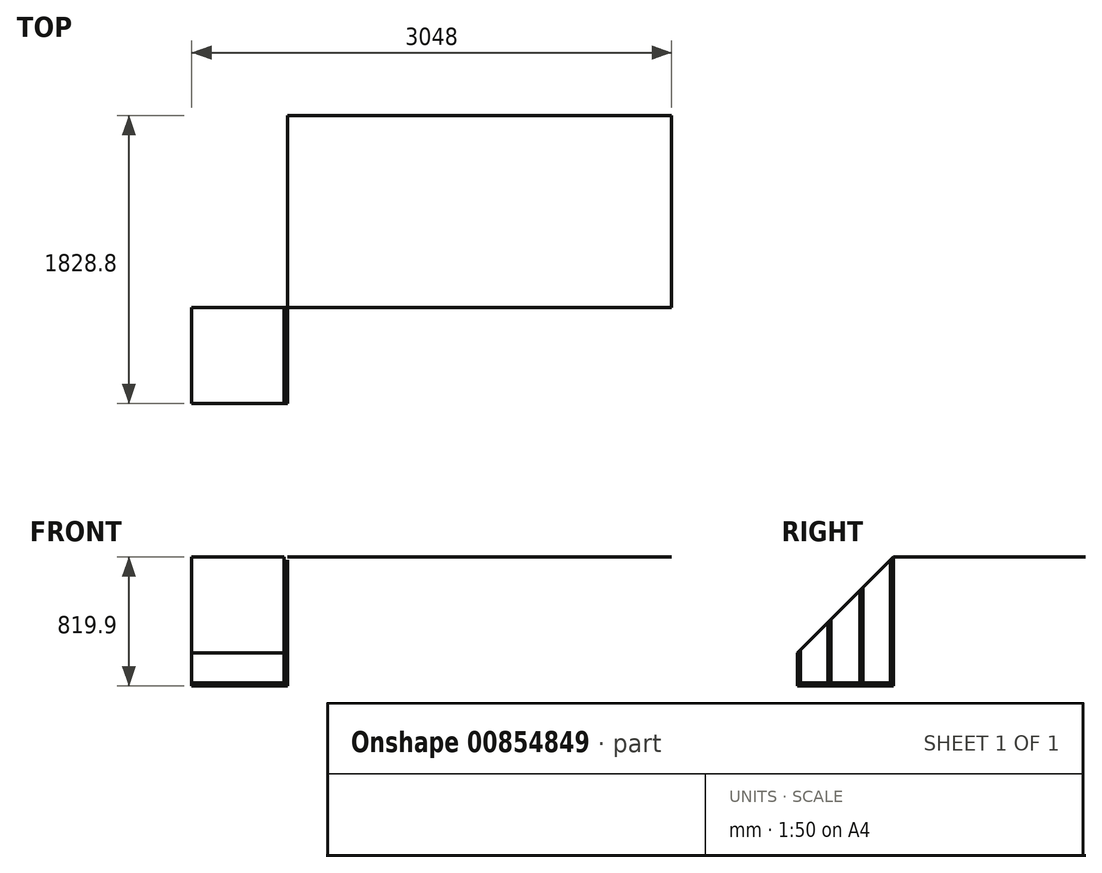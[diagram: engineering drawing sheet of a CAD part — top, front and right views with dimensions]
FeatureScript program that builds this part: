
annotation { "Feature Type Name" : "Feature", "Feature Type Description" : "" }
export const myFeature = defineFeature(function(context is Context, id is Id, definition is map)
    precondition{}
    {
        {
            assignVariable(context, id + "F0", {"name" : "t", "anyValue" : .750});
        }
        {
            var Q0;
            Q0=qCreatedBy(makeId("Right.planeOp"),FACE);
            var sketch = newSketch(context, id + "F1", { "sketchPlane" : qUnion([Q0])});
            skLineSegment(sketch, "E0", {"start": v(0, 0) * mm, "end": v(0, -800.1) * mm});
            skLineSegment(sketch, "E1", {"start": v(0, -800.1) * mm, "end": v(-609.6, -800.1) * mm});
            skLineSegment(sketch, "E2", {"start": v(-609.6, -800.1) * mm, "end": v(-609.6, -609.6) * mm});
            skLineSegment(sketch, "E3", {"start": v(-609.6, -609.6) * mm, "end": v(0, 0) * mm});
            skLineSegment(sketch, "E4", {"start": v(-203.2, -800.1) * mm, "end": v(-203.2, -203.2) * mm, "construction": true});
            skLineSegment(sketch, "E5", {"start": v(-406.4, -800.1) * mm, "end": v(-406.4, -406.4) * mm, "construction": true});
            skLineSegment(sketch, "E6", {"start": v(-609.6, -800.1) * mm, "end": v(-609.6, -819.15) * mm});
            skLineSegment(sketch, "E7", {"start": v(-609.6, -819.15) * mm, "end": v(0, -819.15) * mm});
            skLineSegment(sketch, "E8", {"start": v(0, -819.15) * mm, "end": v(0, -800.1) * mm});
            skSolve(sketch);
        }
        {
            var Q0;
            Q0=makeQuery(id+"F1.imprint","IMPRINT",FACE,{"disambiguationData":[TD([[makeQuery(id+"F1.imprint","IMPRINT",EDGE,{"derivedFrom":sQuery(id+"F1.wireOp",EDGE,"E1")}),1.0]])]});
            extrude(context, id + "F2", {"entities" : qUnion([Q0]), "oppositeDirection" : true, "depth" : 609.6 * mm, "offsetDistance" : 25.4 * mm});
        }
        {
            var Q0;
            Q0=makeQuery(id+"F1.imprint","IMPRINT",FACE,{"disambiguationData":[TD([[makeQuery(id+"F1.imprint","IMPRINT",EDGE,{"derivedFrom":sQuery(id+"F1.wireOp",EDGE,"E0")}),-1.0]])]});
            extrude(context, id + "F3", {"entities" : qUnion([Q0]), "oppositeDirection" : true, "depth" : 609.6 * mm, "offsetDistance" : 25.4 * mm, "hasSecondDirection" : true, "secondDirectionOppositeDirection" : true, "secondDirectionDepth" : (24 - getVariable(context, 't')) * mm});
        }
        {
            var Q0;
            Q0=makeQuery(id+"F1.imprint","IMPRINT",FACE,{"disambiguationData":[TD([[makeQuery(id+"F1.imprint","IMPRINT",EDGE,{"derivedFrom":sQuery(id+"F1.wireOp",EDGE,"E0")}),-1.0]])]});
            extrude(context, id + "F4", {"entities" : qUnion([Q0]), "oppositeDirection" : true, "depth" : (getVariable(context, 't')) * mm, "offsetDistance" : 25.4 * mm});
        }
        {
            var Q0;
            {var subQ0=sQuery(id+"F1.wireOp",EDGE,"E1");Q0=makeQuery(id+"F4.boolean.opBoolean","MERGE",FACE,{"derivedFrom":[makeQuery(id+"F2.opExtrude","CAP_FACE",FACE,{"disambiguationData":[OSD([subQ0,sQuery(id+"F1.wireOp",EDGE,"E6"),sQuery(id+"F1.wireOp",EDGE,"E7"),sQuery(id+"F1.wireOp",EDGE,"E8")])],"isStart":true}),makeQuery(id+"F4.opExtrude","CAP_FACE",FACE,{"disambiguationData":[OSD([sQuery(id+"F1.wireOp",EDGE,"E0"),subQ0,sQuery(id+"F1.wireOp",EDGE,"E2"),sQuery(id+"F1.wireOp",EDGE,"E3")])],"isStart":true})]});}
            var sketch = newSketch(context, id + "F5", { "sketchPlane" : qUnion([Q0])});
            skLineSegment(sketch, "E9", {"start": v(0, 0) * mm, "end": v(0, -800.1) * mm});
            skLineSegment(sketch, "E10", {"start": v(-19.05, -800.1) * mm, "end": v(-19.05, -19.05) * mm});
            skLineSegment(sketch, "E11", {"start": v(-19.05, -19.05) * mm, "end": v(0, 0) * mm});
            skLineSegment(sketch, "E12", {"start": v(0, -800.1) * mm, "end": v(-19.05, -800.1) * mm});
            skLineSegment(sketch, "E13", {"start": v(-609.6, -800.1) * mm, "end": v(-590.55, -800.1) * mm});
            skLineSegment(sketch, "E14", {"start": v(-590.55, -800.1) * mm, "end": v(-590.55, -590.55) * mm});
            skLineSegment(sketch, "E15", {"start": v(-609.6, -800.1) * mm, "end": v(-609.6, -609.6) * mm});
            skLineSegment(sketch, "E16", {"start": v(-609.6, -609.6) * mm, "end": v(-590.55, -590.55) * mm});
            skLineSegment(sketch, "E17", {"start": v(-406.4, -800.1) * mm, "end": v(-406.4, -406.4) * mm, "construction": true});
            skLineSegment(sketch, "E18", {"start": v(-203.2, -800.1) * mm, "end": v(-203.2, -203.2) * mm, "construction": true});
            skLineSegment(sketch, "E19", {"start": v(-406.4, -800.1) * mm, "end": v(-396.88, -800.1) * mm});
            skLineSegment(sketch, "E20", {"start": v(-406.4, -800.1) * mm, "end": v(-415.92, -800.1) * mm});
            skLineSegment(sketch, "E21", {"start": v(-415.92, -800.1) * mm, "end": v(-415.93, -415.93) * mm});
            skLineSegment(sketch, "E22", {"start": v(-396.87, -800.1) * mm, "end": v(-396.87, -396.88) * mm});
            skLineSegment(sketch, "E23", {"start": v(-396.88, -396.88) * mm, "end": v(-415.93, -415.93) * mm});
            skLineSegment(sketch, "E24", {"start": v(-203.2, -800.1) * mm, "end": v(-193.67, -800.1) * mm});
            skLineSegment(sketch, "E25", {"start": v(-203.2, -800.1) * mm, "end": v(-212.73, -800.1) * mm});
            skLineSegment(sketch, "E26", {"start": v(-212.73, -800.1) * mm, "end": v(-212.73, -212.73) * mm});
            skLineSegment(sketch, "E27", {"start": v(-193.68, -800.1) * mm, "end": v(-193.68, -193.68) * mm});
            skLineSegment(sketch, "E28", {"start": v(-193.68, -193.68) * mm, "end": v(-212.73, -212.73) * mm});
            skSolve(sketch);
        }
        {
            var Q0;
            Q0=makeQuery(id+"F5.imprint","IMPRINT",FACE,{"disambiguationData":[TD([[makeQuery(id+"F5.imprint","IMPRINT",EDGE,{"derivedFrom":sQuery(id+"F5.wireOp",EDGE,"E9")}),1.0]])]});
            var Q1;
            Q1=makeQuery(id+"F5.imprint","IMPRINT",FACE,{"disambiguationData":[TD([[makeQuery(id+"F5.imprint","IMPRINT",EDGE,{"derivedFrom":sQuery(id+"F5.wireOp",EDGE,"E9")}),-1.0]])]});
            extrude(context, id + "F6", {"entities" : qUnion([Q0, Q1]), "oppositeDirection" : true, "depth" : (24 - getVariable(context, 't') + 3 / 16) * mm, "offsetDistance" : 25.4 * mm, "hasSecondDirection" : true, "secondDirectionOppositeDirection" : true, "secondDirectionDepth" : (getVariable(context, 't') - 3 / 16) * mm});
        }
        {
            var Q0;
            Q0=makeQuery(id+"F5.imprint","IMPRINT",FACE,{"disambiguationData":[TD([[makeQuery(id+"F5.imprint","IMPRINT",EDGE,{"derivedFrom":sQuery(id+"F5.wireOp",EDGE,"E13")}),-1.0]])]});
            extrude(context, id + "F7", {"entities" : qUnion([Q0]), "oppositeDirection" : true, "depth" : (24 - getVariable(context, 't') + 3 / 16) * mm, "offsetDistance" : 25.4 * mm, "hasSecondDirection" : true, "secondDirectionOppositeDirection" : true, "secondDirectionDepth" : (getVariable(context, 't') - 3 / 16) * mm});
        }
        {
            var Q0;
            Q0=makeQuery(id+"F5.imprint","IMPRINT",FACE,{"disambiguationData":[TD([[makeQuery(id+"F5.imprint","IMPRINT",EDGE,{"derivedFrom":sQuery(id+"F5.wireOp",EDGE,"E19")}),-1.0]])]});
            extrude(context, id + "F8", {"entities" : qUnion([Q0]), "oppositeDirection" : true, "depth" : (24 - getVariable(context, 't') + 3 / 16) * mm, "offsetDistance" : 25.4 * mm, "hasSecondDirection" : true, "secondDirectionOppositeDirection" : true, "secondDirectionDepth" : (getVariable(context, 't') - 3 / 16) * mm});
        }
        {
            var Q0;
            Q0=makeQuery(id+"F5.imprint","IMPRINT",FACE,{"disambiguationData":[TD([[makeQuery(id+"F5.imprint","IMPRINT",EDGE,{"derivedFrom":sQuery(id+"F5.wireOp",EDGE,"E24")}),-1.0]])]});
            extrude(context, id + "F9", {"entities" : qUnion([Q0]), "oppositeDirection" : true, "depth" : (24 - getVariable(context, 't') + 3 / 16) * mm, "offsetDistance" : 25.4 * mm, "hasSecondDirection" : true, "secondDirectionOppositeDirection" : true, "secondDirectionDepth" : (getVariable(context, 't') - 3 / 16) * mm});
        }
        {
            var Q0;
            Q0=makeQuery(id+"F5.imprint","IMPRINT",FACE,{"disambiguationData":[TD([[makeQuery(id+"F5.imprint","IMPRINT",EDGE,{"derivedFrom":sQuery(id+"F5.wireOp",EDGE,"E13")}),-1.0]])]});
            var Q1;
            Q1=makeQuery(id+"F5.imprint","IMPRINT",FACE,{"disambiguationData":[TD([[makeQuery(id+"F5.imprint","IMPRINT",EDGE,{"derivedFrom":sQuery(id+"F5.wireOp",EDGE,"E19")}),-1.0]])]});
            var Q2;
            Q2=makeQuery(id+"F5.imprint","IMPRINT",FACE,{"disambiguationData":[TD([[makeQuery(id+"F5.imprint","IMPRINT",EDGE,{"derivedFrom":sQuery(id+"F5.wireOp",EDGE,"E24")}),-1.0]])]});
            var Q3;
            Q3=makeQuery(id+"F5.imprint","IMPRINT",FACE,{"disambiguationData":[TD([[makeQuery(id+"F5.imprint","IMPRINT",EDGE,{"derivedFrom":sQuery(id+"F5.wireOp",EDGE,"E9")}),-1.0]])]});
            extrude(context, id + "F10", {"entities" : qUnion([Q0, Q1, Q2, Q3]), "operationType" : NewBodyOperationType.REMOVE, "oppositeDirection" : true, "depth" : (24 - getVariable(context, 't') + 3 / 16) * mm, "offsetDistance" : 25.4 * mm});
        }
        {
            var Q0;
            Q0=makeQuery(id+"F5.imprint","IMPRINT",FACE,{"disambiguationData":[TD([[makeQuery(id+"F5.imprint","IMPRINT",EDGE,{"derivedFrom":sQuery(id+"F5.wireOp",EDGE,"E13")}),-1.0]])]});
            var Q1;
            Q1=makeQuery(id+"F5.imprint","IMPRINT",FACE,{"disambiguationData":[TD([[makeQuery(id+"F5.imprint","IMPRINT",EDGE,{"derivedFrom":sQuery(id+"F5.wireOp",EDGE,"E19")}),-1.0]])]});
            var Q2;
            Q2=makeQuery(id+"F5.imprint","IMPRINT",FACE,{"disambiguationData":[TD([[makeQuery(id+"F5.imprint","IMPRINT",EDGE,{"derivedFrom":sQuery(id+"F5.wireOp",EDGE,"E24")}),-1.0]])]});
            var Q3;
            Q3=makeQuery(id+"F5.imprint","IMPRINT",FACE,{"disambiguationData":[TD([[makeQuery(id+"F5.imprint","IMPRINT",EDGE,{"derivedFrom":sQuery(id+"F5.wireOp",EDGE,"E9")}),-1.0]])]});
            extrude(context, id + "F11", {"entities" : qUnion([Q0, Q1, Q2, Q3]), "operationType" : NewBodyOperationType.REMOVE, "oppositeDirection" : true, "depth" : (getVariable(context, 't')) * mm, "offsetDistance" : 25.4 * mm, "hasSecondDirection" : true, "secondDirectionOppositeDirection" : true, "secondDirectionDepth" : (getVariable(context, 't') - 3 / 16) * mm});
        }
        {
            var Q0;
            Q0=makeQuery(id+"F4.opExtrude","CAP_FACE",FACE,{"disambiguationData":[OSD([sQuery(id+"F1.wireOp",EDGE,"E0"),sQuery(id+"F1.wireOp",EDGE,"E1"),sQuery(id+"F1.wireOp",EDGE,"E2"),sQuery(id+"F1.wireOp",EDGE,"E3")])],"isStart":true});
            var sketch = newSketch(context, id + "F12", { "sketchPlane" : qUnion([Q0])});
            skLineSegment(sketch, "E29", {"start": v(0, -800.1) * mm, "end": v(0, 0) * mm, "construction": true});
            skLineSegment(sketch, "E30", {"start": v(-14.29, -800.1) * mm, "end": v(-14.29, -14.29) * mm});
            skLineSegment(sketch, "E31", {"start": v(-14.29, -14.29) * mm, "end": v(-198.44, -198.44) * mm});
            skLineSegment(sketch, "E32", {"start": v(-198.44, -198.44) * mm, "end": v(-198.44, -800.1) * mm});
            skLineSegment(sketch, "E33", {"start": v(-198.44, -800.1) * mm, "end": v(-14.29, -800.1) * mm});
            skLineSegment(sketch, "E34", {"start": v(-203.2, -203.2) * mm, "end": v(-203.2, -800.1) * mm, "construction": true});
            skLineSegment(sketch, "E35", {"start": v(-406.4, -800.1) * mm, "end": v(-406.4, -406.4) * mm, "construction": true});
            skLineSegment(sketch, "E36", {"start": v(-207.96, -800.1) * mm, "end": v(-207.96, -207.96) * mm});
            skLineSegment(sketch, "E37", {"start": v(-207.96, -207.96) * mm, "end": v(-401.64, -401.64) * mm});
            skLineSegment(sketch, "E38", {"start": v(-401.64, -401.64) * mm, "end": v(-401.64, -800.1) * mm});
            skLineSegment(sketch, "E39", {"start": v(-401.64, -800.1) * mm, "end": v(-207.96, -800.1) * mm});
            skLineSegment(sketch, "E40", {"start": v(-411.16, -411.16) * mm, "end": v(-411.16, -800.1) * mm});
            skLineSegment(sketch, "E41", {"start": v(-411.16, -800.1) * mm, "end": v(-595.31, -800.1) * mm});
            skLineSegment(sketch, "E42", {"start": v(-595.31, -800.1) * mm, "end": v(-595.31, -595.31) * mm});
            skLineSegment(sketch, "E43", {"start": v(-595.31, -595.31) * mm, "end": v(-411.16, -411.16) * mm});
            skSolve(sketch);
        }
        {
            var Q0;
            Q0=makeQuery(id+"F12.imprint","IMPRINT",FACE,{"disambiguationData":[TD([[makeQuery(id+"F12.imprint","IMPRINT",EDGE,{"derivedFrom":sQuery(id+"F12.wireOp",EDGE,"E40")}),-1.0]])]});
            var Q1;
            Q1=makeQuery(id+"F12.imprint","IMPRINT",FACE,{"disambiguationData":[TD([[makeQuery(id+"F12.imprint","IMPRINT",EDGE,{"derivedFrom":sQuery(id+"F12.wireOp",EDGE,"E36")}),1.0]])]});
            var Q2;
            Q2=makeQuery(id+"F12.imprint","IMPRINT",FACE,{"disambiguationData":[TD([[makeQuery(id+"F12.imprint","IMPRINT",EDGE,{"derivedFrom":sQuery(id+"F12.wireOp",EDGE,"E30")}),1.0]])]});
            extrude(context, id + "F13", {"entities" : qUnion([Q0, Q1, Q2]), "oppositeDirection" : true, "depth" : (16 + getVariable(context, 't') / 2) * mm, "offsetDistance" : 25.4 * mm, "hasSecondDirection" : true, "secondDirectionOppositeDirection" : true, "secondDirectionDepth" : (16 - getVariable(context, 't') / 2) * mm});
        }
        {
            var Q0;
            Q0=makeQuery(id+"F12.imprint","IMPRINT",FACE,{"disambiguationData":[TD([[makeQuery(id+"F12.imprint","IMPRINT",EDGE,{"derivedFrom":sQuery(id+"F12.wireOp",EDGE,"E40")}),-1.0]])]});
            var Q1;
            Q1=makeQuery(id+"F12.imprint","IMPRINT",FACE,{"disambiguationData":[TD([[makeQuery(id+"F12.imprint","IMPRINT",EDGE,{"derivedFrom":sQuery(id+"F12.wireOp",EDGE,"E36")}),1.0]])]});
            var Q2;
            Q2=makeQuery(id+"F12.imprint","IMPRINT",FACE,{"disambiguationData":[TD([[makeQuery(id+"F12.imprint","IMPRINT",EDGE,{"derivedFrom":sQuery(id+"F12.wireOp",EDGE,"E30")}),1.0]])]});
            extrude(context, id + "F14", {"entities" : qUnion([Q0, Q1, Q2]), "oppositeDirection" : true, "depth" : (8 + getVariable(context, 't') / 2) * mm, "offsetDistance" : 25.4 * mm, "hasSecondDirection" : true, "secondDirectionOppositeDirection" : true, "secondDirectionDepth" : (8 - getVariable(context, 't') / 2) * mm});
        }
        {
            var Q0;
            Q0=makeQuery(id+"F12.imprint","IMPRINT",FACE,{"disambiguationData":[TD([[makeQuery(id+"F12.imprint","IMPRINT",EDGE,{"derivedFrom":sQuery(id+"F12.wireOp",EDGE,"E40")}),-1.0]])]});
            var Q1;
            Q1=makeQuery(id+"F12.imprint","IMPRINT",FACE,{"disambiguationData":[TD([[makeQuery(id+"F12.imprint","IMPRINT",EDGE,{"derivedFrom":sQuery(id+"F12.wireOp",EDGE,"E36")}),1.0]])]});
            var Q2;
            Q2=makeQuery(id+"F12.imprint","IMPRINT",FACE,{"disambiguationData":[TD([[makeQuery(id+"F12.imprint","IMPRINT",EDGE,{"derivedFrom":sQuery(id+"F12.wireOp",EDGE,"E30")}),1.0]])]});
            extrude(context, id + "F15", {"entities" : qUnion([Q0, Q1, Q2]), "operationType" : NewBodyOperationType.REMOVE, "oppositeDirection" : true, "depth" : (16 + getVariable(context, 't') / 2) * mm, "offsetDistance" : 25.4 * mm, "hasSecondDirection" : true, "secondDirectionOppositeDirection" : true, "secondDirectionDepth" : (16 - getVariable(context, 't') / 2) * mm});
        }
        {
            var Q0;
            Q0=makeQuery(id+"F12.imprint","IMPRINT",FACE,{"disambiguationData":[TD([[makeQuery(id+"F12.imprint","IMPRINT",EDGE,{"derivedFrom":sQuery(id+"F12.wireOp",EDGE,"E40")}),-1.0]])]});
            var Q1;
            Q1=makeQuery(id+"F12.imprint","IMPRINT",FACE,{"disambiguationData":[TD([[makeQuery(id+"F12.imprint","IMPRINT",EDGE,{"derivedFrom":sQuery(id+"F12.wireOp",EDGE,"E36")}),1.0]])]});
            var Q2;
            Q2=makeQuery(id+"F12.imprint","IMPRINT",FACE,{"disambiguationData":[TD([[makeQuery(id+"F12.imprint","IMPRINT",EDGE,{"derivedFrom":sQuery(id+"F12.wireOp",EDGE,"E30")}),1.0]])]});
            extrude(context, id + "F16", {"entities" : qUnion([Q0, Q1, Q2]), "operationType" : NewBodyOperationType.REMOVE, "oppositeDirection" : true, "depth" : (8 + getVariable(context, 't') / 2) * mm, "offsetDistance" : 25.4 * mm, "hasSecondDirection" : true, "secondDirectionOppositeDirection" : true, "secondDirectionDepth" : (8 - getVariable(context, 't') / 2) * mm});
        }
        {
            var Q0;
            Q0=makeQuery(id+"F2.opExtrude","SWEPT_BODY",BODY,{"disambiguationData":[OSD([sQuery(id+"F1.wireOp",EDGE,"E1"),sQuery(id+"F1.wireOp",EDGE,"E6"),sQuery(id+"F1.wireOp",EDGE,"E7"),sQuery(id+"F1.wireOp",EDGE,"E8")])]});
            transform(context, id + "F17", {"entities" : qUnion([Q0]), "transformType" : TransformType.TRANSLATION_3D, "dx" : 1219.2 * mm, "dy" : 0 * mm, "dz" : 0 * mm, "makeCopy" : true});
        }
        {
            var Q0;
            Q0=makeQuery(id+"F3.opExtrude","SWEPT_BODY",BODY,{"disambiguationData":[OSD([sQuery(id+"F1.wireOp",EDGE,"E0"),sQuery(id+"F1.wireOp",EDGE,"E1"),sQuery(id+"F1.wireOp",EDGE,"E2"),sQuery(id+"F1.wireOp",EDGE,"E3")])]});
            transform(context, id + "F18", {"entities" : qUnion([Q0]), "transformType" : TransformType.TRANSLATION_3D, "dx" : 863.6 * mm, "dy" : 0 * mm, "dz" : 0 * mm, "makeCopy" : true});
        }
        {
            var Q0;
            Q0=makeQuery(id+"F17.opPattern","COPY",BODY,{"derivedFrom":makeQuery(id+"F2.opExtrude","SWEPT_BODY",BODY,{"disambiguationData":[OSD([sQuery(id+"F1.wireOp",EDGE,"E1"),sQuery(id+"F1.wireOp",EDGE,"E6"),sQuery(id+"F1.wireOp",EDGE,"E7"),sQuery(id+"F1.wireOp",EDGE,"E8")])]}),"instanceName":"1"});
            deleteBodies(context, id + "F19", {"entities" : qUnion([Q0])});
        }
        {
            var Q0;
            Q0=makeQuery(id+"F18.opPattern","COPY",BODY,{"derivedFrom":makeQuery(id+"F3.opExtrude","SWEPT_BODY",BODY,{"disambiguationData":[OSD([sQuery(id+"F1.wireOp",EDGE,"E0"),sQuery(id+"F1.wireOp",EDGE,"E1"),sQuery(id+"F1.wireOp",EDGE,"E2"),sQuery(id+"F1.wireOp",EDGE,"E3")])]}),"instanceName":"1"});
            deleteBodies(context, id + "F20", {"entities" : qUnion([Q0])});
        }
        {
            var Q0;
            Q0=qCreatedBy(makeId("Top.planeOp"),FACE);
            var sketch = newSketch(context, id + "F21", { "sketchPlane" : qUnion([Q0])});
            skLineSegment(sketch, "E44.bottom", {"start": v(0, 0) * mm, "end": v(2438.4, 0) * mm});
            skLineSegment(sketch, "E44.top", {"start": v(0, 1219.2) * mm, "end": v(2438.4, 1219.2) * mm});
            skLineSegment(sketch, "E44.left", {"start": v(0, 0) * mm, "end": v(0, 1219.2) * mm});
            skLineSegment(sketch, "E44.right", {"start": v(2438.4, 0) * mm, "end": v(2438.4, 1219.2) * mm});
            skSolve(sketch);
        }
        {
            var Q0;
            Q0=makeQuery(id+"F21.imprint","IMPRINT",FACE,{"disambiguationData":[TD([[makeQuery(id+"F21.imprint","IMPRINT",EDGE,{"derivedFrom":sQuery(id+"F21.wireOp",EDGE,"E44.bottom")}),1.0]])]});
            extrude(context, id + "F22", {"entities" : qUnion([Q0]), "depth" : (getVariable(context, 't')) * mm, "offsetDistance" : 25.4 * mm});
        }
    });
